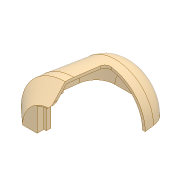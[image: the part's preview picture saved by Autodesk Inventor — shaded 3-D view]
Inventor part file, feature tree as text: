
AUTODESK INVENTOR PART (.ipt)
format: ipt  version: 2017 (Build 210142000, 142)  size: 495,104 bytes
history: native  units: mm
features: sketch x20, extrude x15, projected_geometry x8, fillet x6, chamfer x3, plane x2, revolve x1, thicken_offset x1, shell x1
ambient origin geometry x8: Origin, YZ Plane, XZ Plane, XY Plane, X Axis, Y Axis, Z Axis, Center Point
bodies: Solid1 (feature_tree)
feature tree (57):
  revolve  "Revolution1"  [1 undecoded]
  fillet  "Fillet1"  Radius=30.0mm
  chamfer  "Chamfer1"  Distance=10.0mm Angle=45.0deg
  fillet  "Fillet2"  Radius=20.0mm
  fillet  "Fillet3"  Radius=60.0mm
  thicken_offset  "Thicken1"
  extrude  "Extrusion1"  Depth=4.0mm
  sketch  "Sketch3"  dims[d4=20.0mm d5=10.0mm d6=20.0mm d7=45.0deg d8=20.0mm d9=60.0mm]
  extrude  "Extrusion5"  Depth=50.0mm
  sketch  "Sketch7"  dims[d12=0.0mm d13=0.0mm d14=50.0mm]
  plane  "Work Plane1"
  extrude  "Extrusion6"  Depth=12.0mm
  extrude  "Extrusion7"  Depth=12.0mm
  extrude  "Extrusion8"  Depth=40.0mm
  plane  "Work Plane2"
  extrude  "Extrusion9"  Depth=22.0mm
  sketch  "Sketch12"  dims[d39=4.0mm d40=6.0mm]
  extrude  "Extrusion10"  Depth=4.0mm
  extrude  "Extrusion11"  Depth=20.5mm TaperAngle=0.0deg
  chamfer  "Chamfer2"  Distance=6.0mm
  shell  "Shell2"  Thickness=12.0mm
  extrude  "Extrusion12"  Depth=2.0mm TaperAngle=0.0deg
  extrude  "Extrusion13"  Depth=2.0mm TaperAngle=0.0deg
  sketch  "Sketch17"  dims[d55=10.0mm d56=0.0mm d57=0.0mm]
  extrude  "Extrusion14"  TaperAngle=0.0deg  [1 undecoded]
  fillet  "Fillet8"  Radius=2.0mm
  extrude  "Extrusion15"  Depth=10.0mm TaperAngle=0.0deg
  chamfer  "Chamfer3"  Distance=10.0mm
  extrude  "Extrusion16"  Depth=3.0mm
  extrude  "Extrusion17"  Depth=10.0mm TaperAngle=45.0deg
  extrude  "Extrusion18"  TaperAngle=0.0deg  [1 undecoded]
  fillet  "Fillet9"  Radius=6.0mm
  fillet  "Fillet10"  Radius=6.0mm
  sketch  "Sketch1"  dims[d0=40.0mm d1=80.0mm d2=30.0mm]
  sketch  "Sketch2"  dims[d3=90.0deg]
  sketch  "Sketch6"  dims[d10=4.0mm d11=4.0mm]
  sketch  "Sketch8"  dims[d15=12.0mm d16=12.0mm]
  sketch  "Sketch9"  dims[d17=12.0mm d18=12.0mm]
  projected_geometry  "Projected Loop1"
  sketch  "Sketch10"  dims[d34=45.0mm d35=40.0mm]
  projected_geometry  "Projected Loop2"
  sketch  "Sketch11"  dims[d36=40.0mm d37=0.0mm d38=22.0mm]
  sketch  "Sketch13"  dims[d41=-8.0mm d42=20.5mm d43=0.0mm]
  sketch  "Sketch14"  dims[d44=25.0mm d45=6.0mm d46=0.0mm d47=12.0mm d48=0.0mm]
  sketch  "Sketch15"  dims[d49=-3.75mm d50=2.0mm d51=0.0mm]
  projected_geometry  "Projected Loop3"
  sketch  "Sketch16"  dims[d52=28.0mm d53=2.0mm d54=0.0mm]
  projected_geometry  "Projected Loop4"
  sketch  "Sketch18"  dims[d58=11.0mm d59=2.0mm d60=45.0deg d61=2.0mm]
  projected_geometry  "Projected Loop5"
  sketch  "Sketch19"  dims[d62=10.0mm d63=0.0mm d64=10.0mm d65=0.0mm d66=10.0mm d67=0.0mm]
  sketch  "Sketch20"  dims[d68=3.0mm d69=3.0mm]
  sketch  "Sketch21"  dims[d70=10.0mm d71=0.0mm d72=6.0mm d73=2.0mm d74=45.0deg]
  projected_geometry  "Projected Loop6"
  projected_geometry  "Projected Loop7"
  sketch  "Sketch22"  dims[d75=55.0mm d76=0.0mm d77=0.0mm d78=6.0mm d79=0.0mm d80=6.0mm d81=0.0mm d82=4.0mm d83=4.0mm]
  projected_geometry  "Projected Loop8"
note: 3 required parameter values undecoded (feature->parameter linkage not recoverable at this tier; creation-order binding heuristic only, values carry confidence <= 0.55)